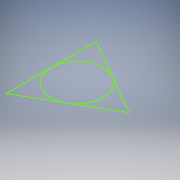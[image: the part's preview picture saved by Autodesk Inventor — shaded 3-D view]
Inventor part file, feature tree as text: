
AUTODESK INVENTOR PART (.ipt)
format: ipt  version: 2018 (Build 220112000, 112)  size: 84,992 bytes
history: native  units: in
note: dims shown in document units (in); Inventor stores cm internally (conversion verified against a paired STEP export)
features: sketch x1
ambient origin geometry x8: Origin, YZ Plane, XZ Plane, XY Plane, X Axis, Y Axis, Z Axis, Center Point
feature tree (1):
  sketch  "Sketch1"
